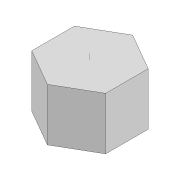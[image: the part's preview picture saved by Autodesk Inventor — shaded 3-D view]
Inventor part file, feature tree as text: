
AUTODESK INVENTOR PART (.ipt)
format: ipt  version: 2022 (Build 260153000, 153)  size: 80,896 bytes
history: native  units: mm
features: extrude x1, sketch x1
ambient origin geometry x8: Origin, YZ Plane, XZ Plane, XY Plane, X Axis, Y Axis, Z Axis, Center Point
bodies: Solid1 (feature_tree)
feature tree (2):
  extrude  "Extrusion1"  Depth=4.9mm TaperAngle=0.0deg
  sketch  "Sketch1"  dims[d0=6.9mm d1=4.9mm d2=0.0mm]
